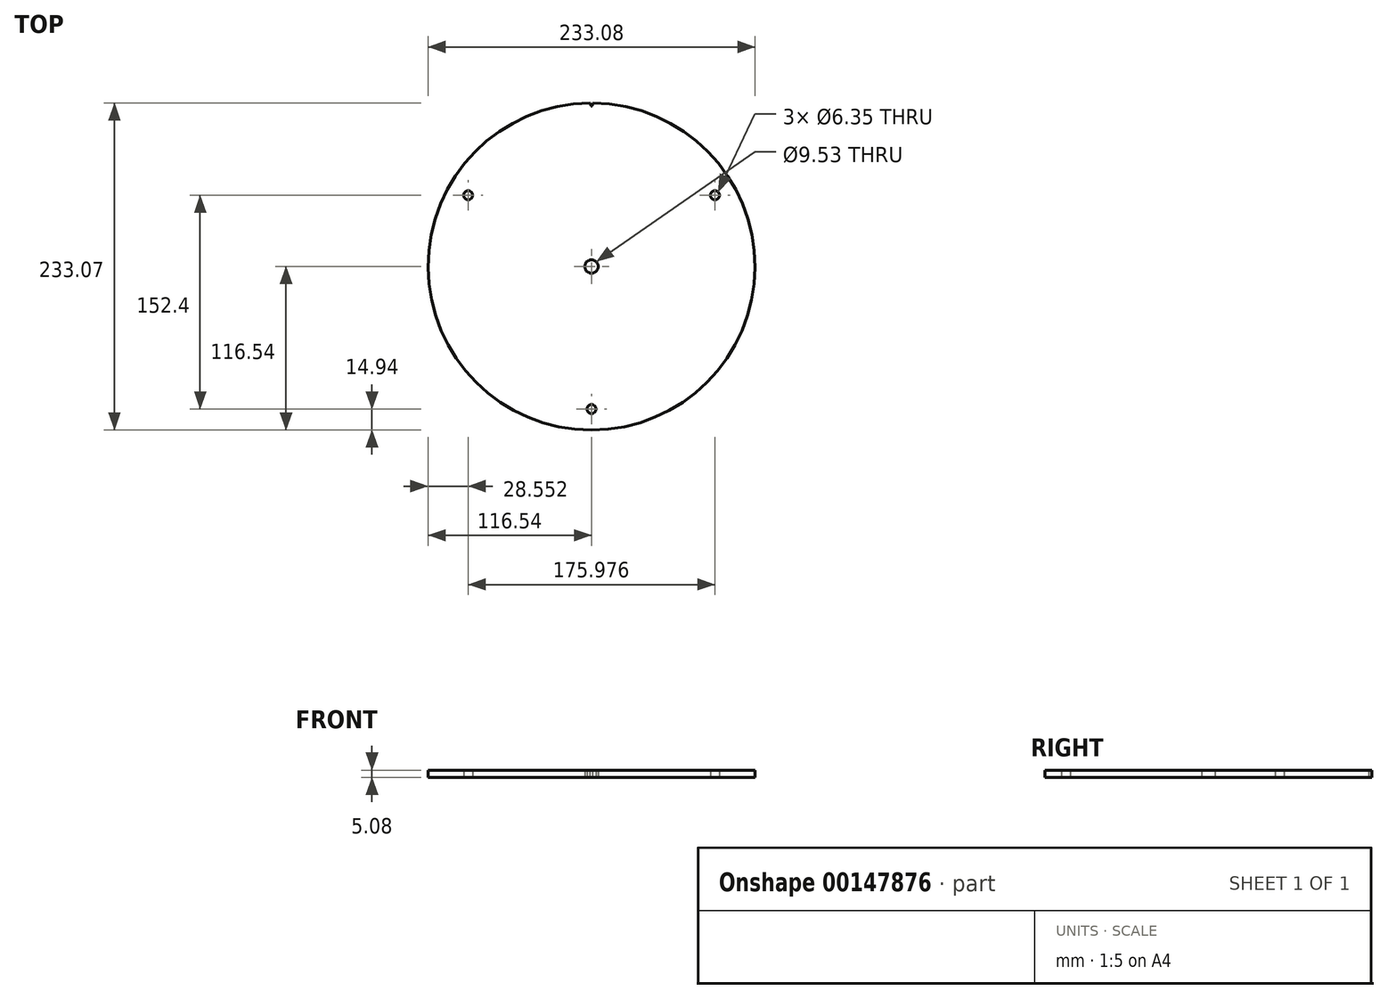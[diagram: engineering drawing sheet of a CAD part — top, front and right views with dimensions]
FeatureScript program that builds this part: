
annotation { "Feature Type Name" : "Feature", "Feature Type Description" : "" }
export const myFeature = defineFeature(function(context is Context, id is Id, definition is map)
    precondition{}
    {
        {
            var Q0;
            Q0=qCreatedBy(makeId("Top.planeOp"),FACE);
            var sketch = newSketch(context, id + "F0", { "sketchPlane" : qUnion([Q0])});
            skCircle(sketch, "E0", {"center": v(0, 0) * mm, "radius": 116.54 * mm});
            skCircle(sketch, "E1", {"center": v(0, 0) * mm, "radius": 4.76 * mm});
            skCircle(sketch, "E2", {"center": v(0, 0) * mm, "radius": 114.3 * mm, "construction": true});
            skCircle(sketch, "E3.cCircle", {"center": v(0, 0) * mm, "radius": 50.8 * mm, "construction": true});
            skLineSegment(sketch, "E3.0", {"start": v(-87.99, 50.8) * mm, "end": v(87.99, 50.8) * mm, "construction": true});
            skLineSegment(sketch, "E3.1", {"start": v(87.99, 50.8) * mm, "end": v(0, -101.6) * mm, "construction": true});
            skLineSegment(sketch, "E3.2", {"start": v(0, -101.6) * mm, "end": v(-87.99, 50.8) * mm, "construction": true});
            skPoint(sketch, "E3.0.midPoint", {"position": v(0, 50.8) * mm});
            skCircle(sketch, "E4", {"center": v(-87.99, 50.8) * mm, "radius": 12.7 * mm, "construction": true});
            skCircle(sketch, "E5", {"center": v(-87.99, 50.8) * mm, "radius": 3.18 * mm});
            skCircle(sketch, "E6", {"center": v(87.99, 50.8) * mm, "radius": 3.18 * mm});
            skCircle(sketch, "E7", {"center": v(0, -101.6) * mm, "radius": 3.18 * mm});
            skSolve(sketch);
        }
        {
            var Q0;
            Q0=makeQuery(id+"F0.imprint","IMPRINT",FACE,{"disambiguationData":[TD([[makeQuery(id+"F0.imprint","IMPRINT",EDGE,{"derivedFrom":sQuery(id+"F0.wireOp",EDGE,"d7zeTPih-CRss-xDOh-gPdP-rmPCdwzH7cdN.left")}),1.0]])]});
            var Q1;
            Q1=makeQuery(id+"F0.imprint","IMPRINT",FACE,{"disambiguationData":[TD([[makeQuery(id+"F0.imprint","IMPRINT",EDGE,{"derivedFrom":sQuery(id+"F0.wireOp",EDGE,"E0")}),1.0]])]});
            extrude(context, id + "F1", {"entities" : qUnion([Q0, Q1]), "depth" : 5.08 * mm});
        }
        {
            var Q0;
            Q0=makeQuery(id+"F1.opExtrude","CAP_FACE",FACE,{"disambiguationData":[OSD([sQuery(id+"F0.wireOp",EDGE,"d7zeTPih-CRss-xDOh-gPdP-rmPCdwzH7cdN.left"),sQuery(id+"F0.wireOp",EDGE,"d7zeTPih-CRss-xDOh-gPdP-rmPCdwzH7cdN.right"),sQuery(id+"F0.wireOp",EDGE,"ScfBMfkV-s1yN-Ls9R-SGr5-fEyGpD6zak8e"),sQuery(id+"F0.wireOp",EDGE,"xnxmVwjl-FvSF-m7sj-be2U-u85gZZGoORGZ"),sQuery(id+"F0.wireOp",EDGE,"E0")])],"isStart":false});
            var sketch = newSketch(context, id + "F2", { "sketchPlane" : qUnion([Q0])});
            skLineSegment(sketch, "E8", {"start": v(0, 0) * mm, "end": v(0, 116.54) * mm, "construction": true});
            skLineSegment(sketch, "E9", {"start": v(0, 0) * mm, "end": v(0.65, 116.53) * mm, "construction": true});
            skArc(sketch, "E10", {"start": v(1, 116.53) * mm, "mid": v(0, 116.54) * mm, "end": v(-1, 116.53) * mm});
            skLineSegment(sketch, "E11", {"start": v(-1, 116.53) * mm, "end": v(-0.28, 114.56) * mm});
            skLineSegment(sketch, "E12", {"start": v(1, 116.53) * mm, "end": v(0.28, 114.56) * mm});
            skPoint(sketch, "E13", {"position": v(0.64, 115.55) * mm});
            skArc(sketch, "E14", {"start": v(-0.28, 114.56) * mm, "mid": v(0, 114.37) * mm, "end": v(0.28, 114.56) * mm});
            skSolve(sketch);
        }
        {
            var Q0;
            Q0=qSketchRegion(id+"F2",true);
            var Q1;
            Q1=makeQuery(id+"F1.opExtrude","CAP_FACE",FACE,{"disambiguationData":[OSD([sQuery(id+"F0.wireOp",EDGE,"d7zeTPih-CRss-xDOh-gPdP-rmPCdwzH7cdN.left"),sQuery(id+"F0.wireOp",EDGE,"d7zeTPih-CRss-xDOh-gPdP-rmPCdwzH7cdN.right"),sQuery(id+"F0.wireOp",EDGE,"ScfBMfkV-s1yN-Ls9R-SGr5-fEyGpD6zak8e"),sQuery(id+"F0.wireOp",EDGE,"xnxmVwjl-FvSF-m7sj-be2U-u85gZZGoORGZ"),sQuery(id+"F0.wireOp",EDGE,"E0")])],"isStart":true});
            extrude(context, id + "F3", {"entities" : qUnion([Q0]), "operationType" : NewBodyOperationType.REMOVE, "endBound" : BoundingType.UP_TO_SURFACE, "oppositeDirection" : true, "endBoundEntityFace" : qUnion([Q1]), "depth" : 25.4 * mm});
        }
    });
